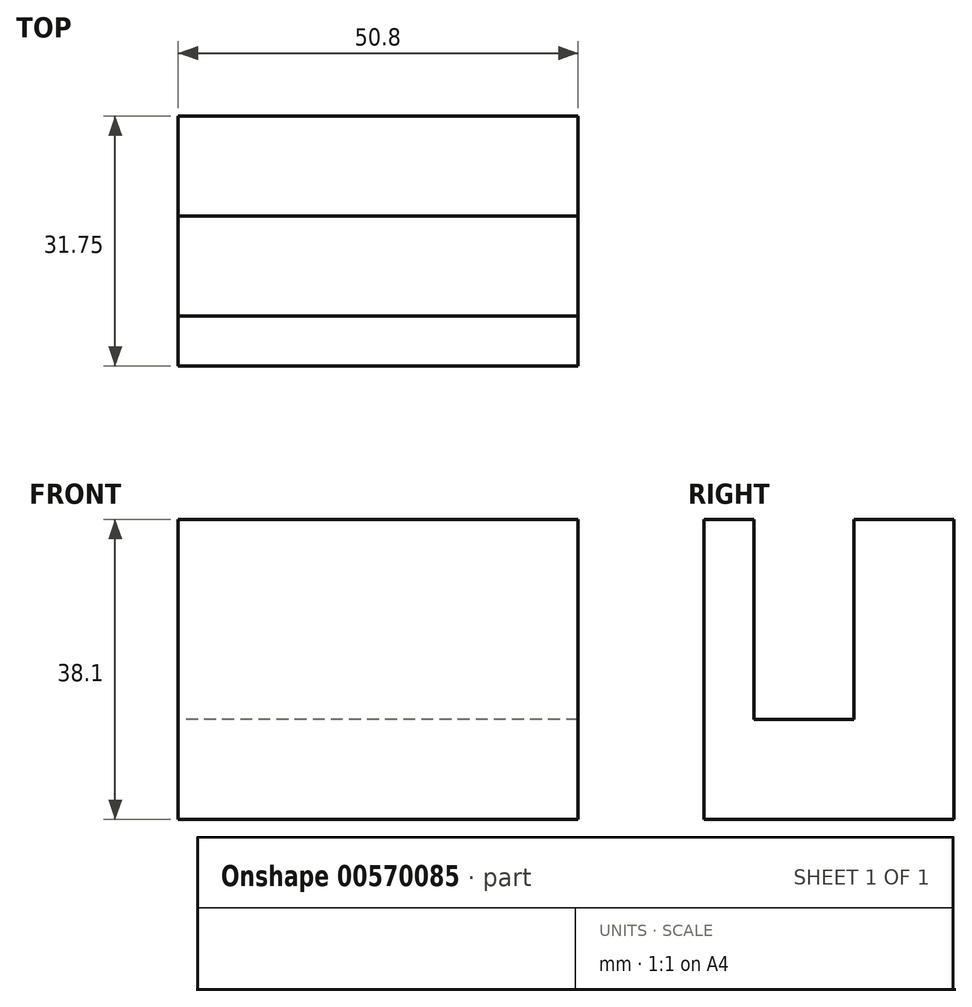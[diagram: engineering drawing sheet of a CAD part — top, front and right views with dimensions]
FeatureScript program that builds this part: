
annotation { "Feature Type Name" : "Feature", "Feature Type Description" : "" }
export const myFeature = defineFeature(function(context is Context, id is Id, definition is map)
    precondition{}
    {
        {
            var Q0;
            Q0=qCreatedBy(makeId("Right.planeOp"),FACE);
            var sketch = newSketch(context, id + "F0", { "sketchPlane" : qUnion([Q0])});
            skLineSegment(sketch, "E0", {"start": v(9.5, -4.34) * mm, "end": v(-22.25, -4.34) * mm});
            skLineSegment(sketch, "E1", {"start": v(-22.25, -4.34) * mm, "end": v(-22.25, 33.76) * mm});
            skLineSegment(sketch, "E2", {"start": v(-22.25, 33.76) * mm, "end": v(-15.9, 33.76) * mm});
            skLineSegment(sketch, "E3", {"start": v(-15.9, 33.76) * mm, "end": v(-15.9, 8.36) * mm});
            skLineSegment(sketch, "E4", {"start": v(9.5, -4.34) * mm, "end": v(9.5, 33.76) * mm});
            skLineSegment(sketch, "E5", {"start": v(-15.9, 8.36) * mm, "end": v(-3.2, 8.36) * mm});
            skLineSegment(sketch, "E6", {"start": v(9.5, 33.76) * mm, "end": v(-3.2, 33.76) * mm});
            skLineSegment(sketch, "E7", {"start": v(-3.2, 33.76) * mm, "end": v(-3.2, 8.36) * mm});
            skSolve(sketch);
        }
        {
            var Q0;
            Q0 = qSketchRegion(id + "F0", true);
            extrude(context, id + "F1", {"entities" : qUnion([Q0]), "depth" : 50.8 * mm, "offsetDistance" : 25.4 * mm});
        }
    });
